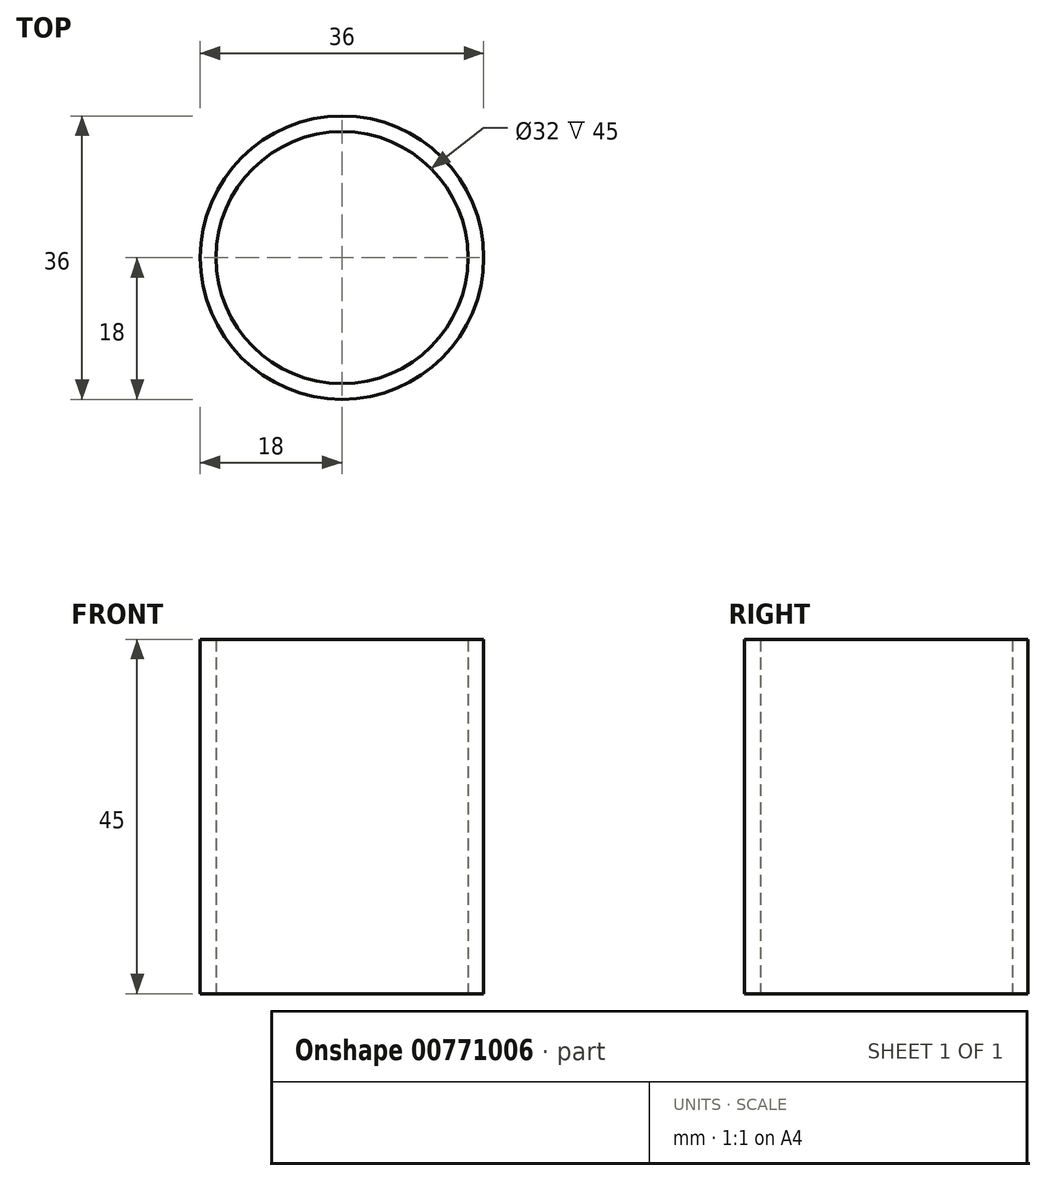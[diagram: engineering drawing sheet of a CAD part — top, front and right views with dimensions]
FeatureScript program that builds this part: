
annotation { "Feature Type Name" : "Feature", "Feature Type Description" : "" }
export const myFeature = defineFeature(function(context is Context, id is Id, definition is map)
    precondition{}
    {
        {
            var Q0;
            Q0=qCreatedBy(makeId("Top.planeOp"),FACE);
            var sketch = newSketch(context, id + "F0", { "sketchPlane" : qUnion([Q0])});
            skCircle(sketch, "E0", {"center": v(0, 0) * mm, "radius": 18 * mm});
            skCircle(sketch, "E1", {"center": v(0, 0) * mm, "radius": 16 * mm});
            skSolve(sketch);
        }
        {
            var Q0;
            Q0 = qSketchRegion(id + "F0", true);
            extrude(context, id + "F1", {"entities" : qUnion([Q0]), "depth" : 45 * mm, "offsetDistance" : 25 * mm});
        }
        {
            var Q0;
            Q0=qCreatedBy(makeId("Front.planeOp"),FACE);
            var sketch = newSketch(context, id + "F2", { "sketchPlane" : qUnion([Q0])});
            skPoint(sketch, "E2", {"position": v(0, 45.19) * mm});
            skPoint(sketch, "E3", {"position": v(0, 29.62) * mm});
            skPoint(sketch, "E4", {"position": v(5.08, 29.62) * mm});
            skPoint(sketch, "E5", {"position": v(5.08, 45.19) * mm});
            skPoint(sketch, "E6", {"position": v(-4.88, 29.62) * mm});
            skPoint(sketch, "E7", {"position": v(-4.88, 45.19) * mm});
            skLineSegment(sketch, "E8", {"start": v(-4.88, 45.19) * mm, "end": v(5.08, 45.19) * mm});
            skLineSegment(sketch, "E9", {"start": v(5.08, 29.62) * mm, "end": v(5.08, 45.19) * mm});
            skLineSegment(sketch, "E10", {"start": v(5.08, 29.62) * mm, "end": v(-4.88, 29.62) * mm});
            skLineSegment(sketch, "E11", {"start": v(-4.96, 29.61) * mm, "end": v(-4.88, 45.19) * mm});
            skLineSegment(sketch, "E12.top", {"start": v(-4.88, 29.62) * mm, "end": v(5.08, 29.62) * mm});
            skLineSegment(sketch, "E12.left", {"start": v(-4.88, 45.19) * mm, "end": v(-4.88, 29.62) * mm});
            skLineSegment(sketch, "E12.right", {"start": v(5.08, 45.19) * mm, "end": v(5.08, 29.62) * mm});
            skSolve(sketch);
        }
        {
            var Q0;
            Q0 = qSketchRegion(id + "F2", true);
            var Q1;
            Q1=sQuery(id+"F2.wireOp",EDGE,"E8");
            var Q2;
            Q2=sQuery(id+"F2.wireOp",EDGE,"E11");
            var Q3;
            Q3=sQuery(id+"F2.wireOp",EDGE,"E9");
            var Q4;
            Q4=sQuery(id+"F2.wireOp",EDGE,"E10");
            extrude(context, id + "F3", {"entities" : qUnion([Q0]), "bodyType" : ToolBodyType.SURFACE, "operationType" : NewBodyOperationType.INTERSECT, "surfaceEntities" : qUnion([Q1, Q2, Q3, Q4]), "oppositeDirection" : true, "depth" : 25 * mm, "offsetDistance" : 25 * mm, "hasSecondDirection" : true, "secondDirectionOppositeDirection" : false, "secondDirectionDepth" : 25 * mm});
        }
    });
